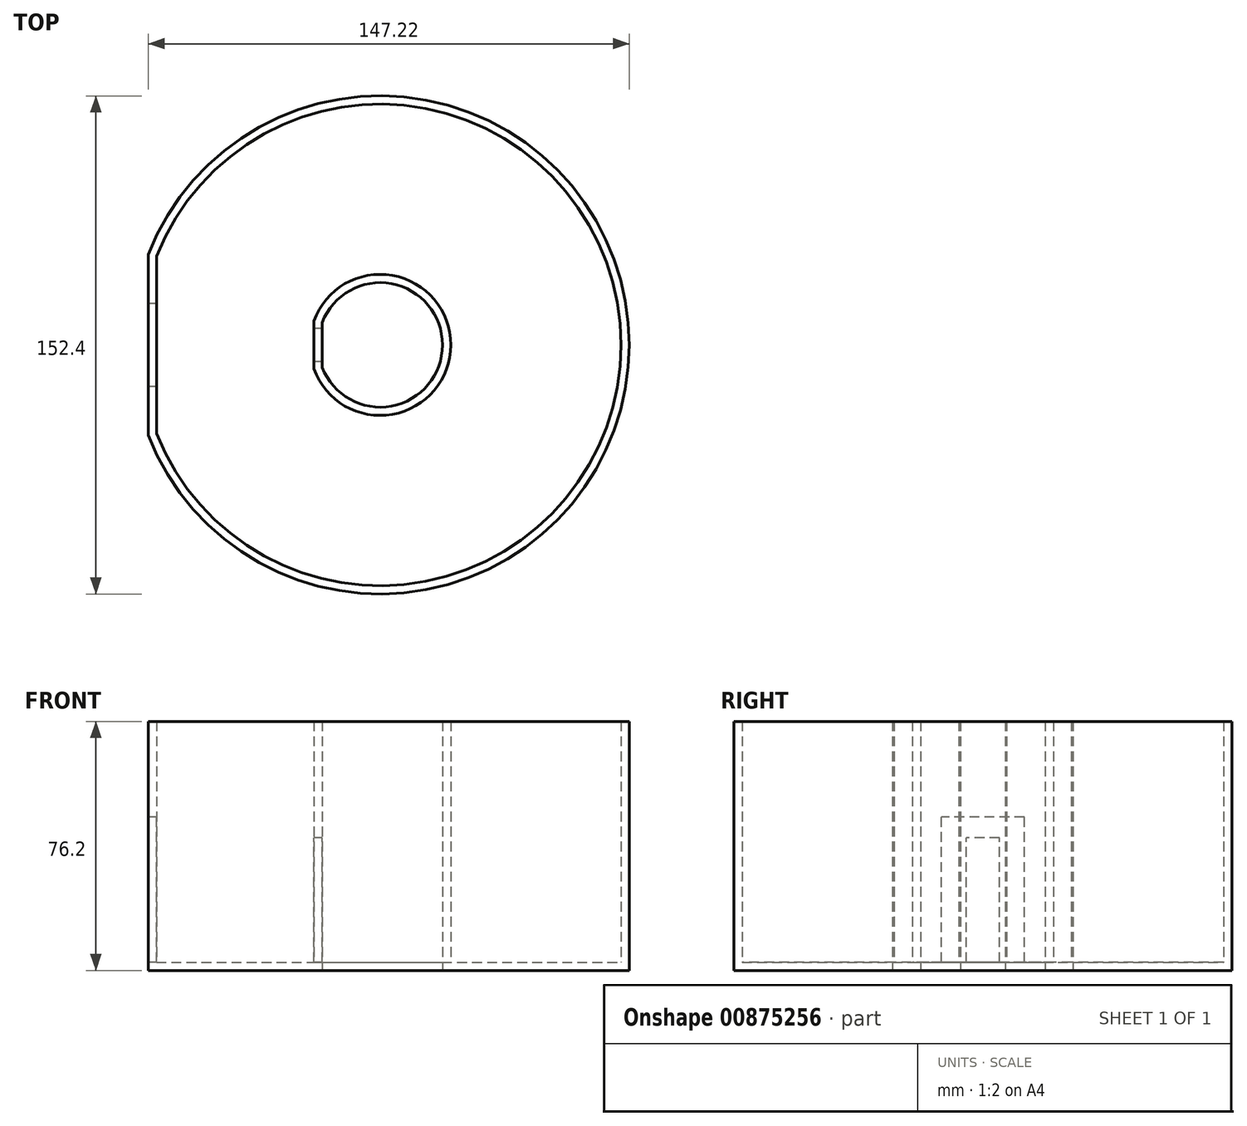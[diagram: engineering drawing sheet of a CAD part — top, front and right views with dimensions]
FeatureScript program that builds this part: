
annotation { "Feature Type Name" : "Feature", "Feature Type Description" : "" }
export const myFeature = defineFeature(function(context is Context, id is Id, definition is map)
    precondition{}
    {
        {
            var Q0;
            Q0=qCreatedBy(makeId("Top.planeOp"),FACE);
            var sketch = newSketch(context, id + "F0", { "sketchPlane" : qUnion([Q0])});
            skCircle(sketch, "E0", {"center": v(0, 0) * mm, "radius": 76.2 * mm});
            skCircle(sketch, "E1", {"center": v(0, 0) * mm, "radius": 19.05 * mm});
            skLineSegment(sketch, "E2", {"start": v(-71.02, 27.6) * mm, "end": v(-71.02, -27.6) * mm});
            skLineSegment(sketch, "E3", {"start": v(-17.77, 6.86) * mm, "end": v(-17.77, -6.86) * mm});
            skPoint(sketch, "E4.endSnap0", {"position": v(-17.77, 0) * mm});
            skSolve(sketch);
        }
        {
            var Q0;
            Q0=makeQuery(id+"F0.imprint","IMPRINT",FACE,{"disambiguationData":[TD([[makeQuery(id+"F0.imprint","IMPRINT",EDGE,{"derivedFrom":sQuery(id+"F0.wireOp",EDGE,"E1")}),-1.0]])]});
            var Q1;
            {var subQ0=sQuery(id+"F0.wireOp",EDGE,"E3");Q1=makeQuery(id+"F0.imprint","IMPRINT",FACE,{"disambiguationData":[TD([[makeQuery(id+"F0.imprint","IMPRINT",EDGE,{"derivedFrom":subQ0}),-1.0]])]});}
            extrude(context, id + "F1", {"entities" : qUnion([Q0, Q1]), "depth" : 76.2 * mm, "offsetDistance" : 25.4 * mm});
        }
        {
            var Q0;
            Q0=makeQuery(id+"F1.opExtrude","CAP_FACE",FACE,{"disambiguationData":[OSD([sQuery(id+"F0.wireOp",EDGE,"E0"),sQuery(id+"F0.wireOp",EDGE,"E1")])],"isStart":false});
            shell(context, id + "F2", {"entities" : qUnion([Q0]), "thickness" : 2.54 * mm});
        }
        {
            var Q0;
            Q0=makeQuery(id+"F1.opExtrude","SWEPT_FACE",FACE,{"disambiguationData":[OSD([sQuery(id+"F0.wireOp",EDGE,"E2")])]});
            var sketch = newSketch(context, id + "F3", { "sketchPlane" : qUnion([Q0])});
            skLineSegment(sketch, "E5.bottom", {"start": v(-12.7, 0) * mm, "end": v(12.7, 0) * mm});
            skLineSegment(sketch, "E5.top", {"start": v(-12.7, 2.54) * mm, "end": v(12.7, 2.54) * mm});
            skLineSegment(sketch, "E5.left", {"start": v(-12.7, 0) * mm, "end": v(-12.7, 2.54) * mm});
            skLineSegment(sketch, "E5.right", {"start": v(12.7, 0) * mm, "end": v(12.7, 2.54) * mm});
            skLineSegment(sketch, "E6.top", {"start": v(-12.7, 47) * mm, "end": v(12.7, 47) * mm});
            skLineSegment(sketch, "E6.left", {"start": v(-12.7, 2.54) * mm, "end": v(-12.7, 47) * mm});
            skLineSegment(sketch, "E6.right", {"start": v(12.7, 2.54) * mm, "end": v(12.7, 47) * mm});
            skSolve(sketch);
        }
        {
            var Q0;
            Q0=makeQuery(id+"F3.imprint","IMPRINT",FACE,{"disambiguationData":[TD([[makeQuery(id+"F3.imprint","IMPRINT",EDGE,{"derivedFrom":sQuery(id+"F3.wireOp",EDGE,"E5.top")}),1.0]])]});
            extrude(context, id + "F4", {"entities" : qUnion([Q0]), "operationType" : NewBodyOperationType.REMOVE, "oppositeDirection" : true, "depth" : 2.54 * mm, "offsetDistance" : 25.4 * mm});
        }
        {
            var Q0;
            Q0=makeQuery(id+"F2.opShell","OFFSET_FACE",FACE,{"disambiguationData":[OSD([sQuery(id+"F0.wireOp",EDGE,"E3")])]});
            var sketch = newSketch(context, id + "F5", { "sketchPlane" : qUnion([Q0])});
            skLineSegment(sketch, "E7.bottom", {"start": v(-5.08, 2.54) * mm, "end": v(5.08, 2.54) * mm});
            skLineSegment(sketch, "E7.top", {"start": v(-5.08, 40.64) * mm, "end": v(5.08, 40.64) * mm});
            skLineSegment(sketch, "E7.left", {"start": v(-5.08, 2.54) * mm, "end": v(-5.08, 40.64) * mm});
            skLineSegment(sketch, "E7.right", {"start": v(5.08, 2.54) * mm, "end": v(5.08, 40.64) * mm});
            skLineSegment(sketch, "E8", {"start": v(-7.32, 2.54) * mm, "end": v(-5.08, 2.54) * mm});
            skLineSegment(sketch, "E9", {"start": v(5.08, 2.54) * mm, "end": v(7.32, 2.54) * mm});
            skLineSegment(sketch, "E10", {"start": v(7.32, 2.54) * mm, "end": v(-7.32, 2.54) * mm});
            skSolve(sketch);
        }
        {
            var Q0;
            Q0=qSketchRegion(id+"F5",true);
            extrude(context, id + "F6", {"entities" : qUnion([Q0]), "operationType" : NewBodyOperationType.REMOVE, "oppositeDirection" : true, "depth" : 2.54 * mm, "offsetDistance" : 25.4 * mm});
        }
    });
